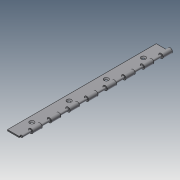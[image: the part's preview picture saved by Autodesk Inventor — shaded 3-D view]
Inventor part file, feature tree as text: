
AUTODESK INVENTOR PART (.ipt)
format: ipt  version: 2018.3 (Build 223284000, 284)  size: 422,912 bytes
history: native  units: in
note: dims shown in document units (in); Inventor stores cm internally (conversion verified against a paired STEP export)
features: extrude x1, sketch x1, chamfer x1, other x1, mirror x1
ambient origin geometry x8: Origin, YZ Plane, XZ Plane, XY Plane, X Axis, Y Axis, Z Axis, Center Point
bodies: Solid1 (feature_tree), Solid2 (feature_tree), Solid3 (feature_tree)
feature tree (5):
  extrude  "Extrusion1"  Depth=4.0in
  sketch  "Sketch1"  dims[d0=4.0in d1=4.0in d2=1.0in d3=0.0in]
  chamfer  "Chamfer1"  Distance=1.0in
  other  "LPattern4"
  mirror  "Mirror3"
